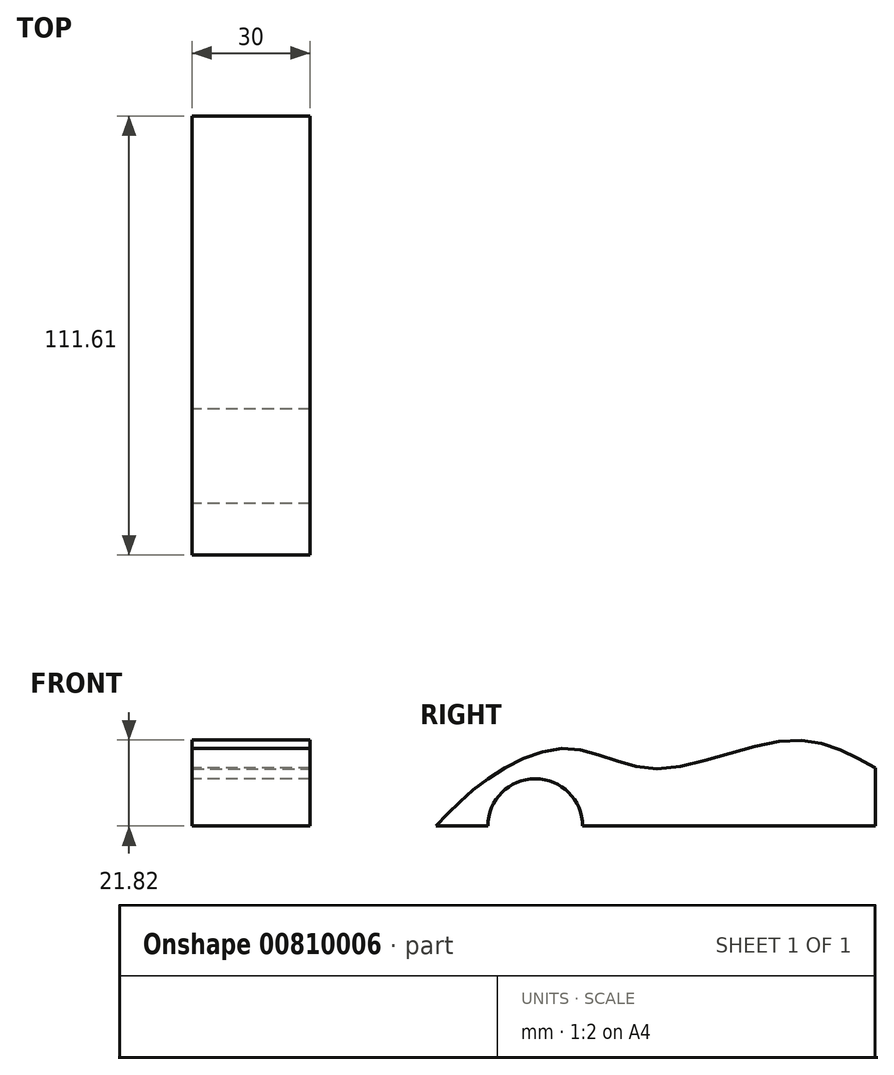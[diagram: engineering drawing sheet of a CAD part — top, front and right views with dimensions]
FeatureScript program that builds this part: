
annotation { "Feature Type Name" : "Feature", "Feature Type Description" : "" }
export const myFeature = defineFeature(function(context is Context, id is Id, definition is map)
    precondition{}
    {
        {
            var Q0;
            Q0=qCreatedBy(makeId("Right.planeOp"),FACE);
            var sketch = newSketch(context, id + "F0", { "sketchPlane" : qUnion([Q0])});
            skLineSegment(sketch, "E0", {"start": v(-55.56, 0) * mm, "end": v(56.05, 0) * mm});
            skLineSegment(sketch, "E1", {"start": v(56.05, 0) * mm, "end": v(56.05, 14.8) * mm});
            skCircle(sketch, "E2", {"center": v(-30.37, 0) * mm, "radius": 12 * mm});
            skCircle(sketch, "E3", {"center": v(40.85, 3.87) * mm, "radius": 12 * mm});
            skFitSpline(sketch, "E4", {"points": [v(-55.56, 0) * mm, v(-42.4, 12) * mm, v(-21.43, 19.69) * mm, v(0, 14.56) * mm, v(34.49, 21.78) * mm, v(56.05, 14.8) * mm], "startDerivative": vector(67.35, 71.02) * mm, "endDerivative": vector(100.38, -56.69) * mm});
            skSolve(sketch);
        }
        {
            var Q0;
            {var subQ0=sQuery(id+"F0.wireOp",EDGE,"E1");Q0=makeQuery(id+"F0.imprint","IMPRINT",FACE,{"disambiguationData":[TD([[makeQuery(id+"F0.imprint","IMPRINT",EDGE,{"derivedFrom":subQ0}),1.0]])]});}
            var Q1;
            {var subQ0=sQuery(id+"F0.wireOp",EDGE,"E2");var subQ1=sQuery(id+"F0.wireOp",EDGE,"E0");var subQ2=makeQuery(id+"F0.imprint","INTERSECT",VERTEX,{"disambiguationData":[OD(0.0)],"derivedFrom":[subQ1,subQ0]});Q1=makeQuery(id+"F0.imprint","IMPRINT",FACE,{"disambiguationData":[TD([[makeQuery(id+"F0.imprint","IMPRINT",EDGE,{"disambiguationData":[TD([[subQ2,-1.0]])],"derivedFrom":subQ1}),1.0]])]});}
            var Q2;
            {var subQ0=sQuery(id+"F0.wireOp",EDGE,"E3");var subQ1=sQuery(id+"F0.wireOp",EDGE,"E0");var subQ2=makeQuery(id+"F0.imprint","INTERSECT",VERTEX,{"disambiguationData":[OD(0.0)],"derivedFrom":[subQ1,subQ0]});Q2=makeQuery(id+"F0.imprint","IMPRINT",FACE,{"disambiguationData":[TD([[makeQuery(id+"F0.imprint","IMPRINT",EDGE,{"disambiguationData":[TD([[subQ2,-1.0]])],"derivedFrom":subQ1}),1.0]])]});}
            extrude(context, id + "F1", {"entities" : qUnion([Q0, Q1, Q2]), "depth" : 15 * mm, "offsetDistance" : 25 * mm});
        }
        {
            var Q0;
            Q0=makeQuery(id+"F1.opExtrude","SWEPT_BODY",BODY,{"disambiguationData":[OSD([sQuery(id+"F0.wireOp",EDGE,"E0"),sQuery(id+"F0.wireOp",EDGE,"E1"),sQuery(id+"F0.wireOp",EDGE,"E4")])]});
            var Q1;
            {var subQ0=sQuery(id+"F0.wireOp",EDGE,"E1");Q1=makeQuery(id+"F0.imprint","IMPRINT",FACE,{"disambiguationData":[TD([[makeQuery(id+"F0.imprint","IMPRINT",EDGE,{"derivedFrom":subQ0}),1.0]])]});}
            mirror(context, id + "F2", {"operationType" : NewBodyOperationType.ADD, "entities" : qUnion([Q0]), "mirrorPlane" : qUnion([Q1])});
        }
    });
